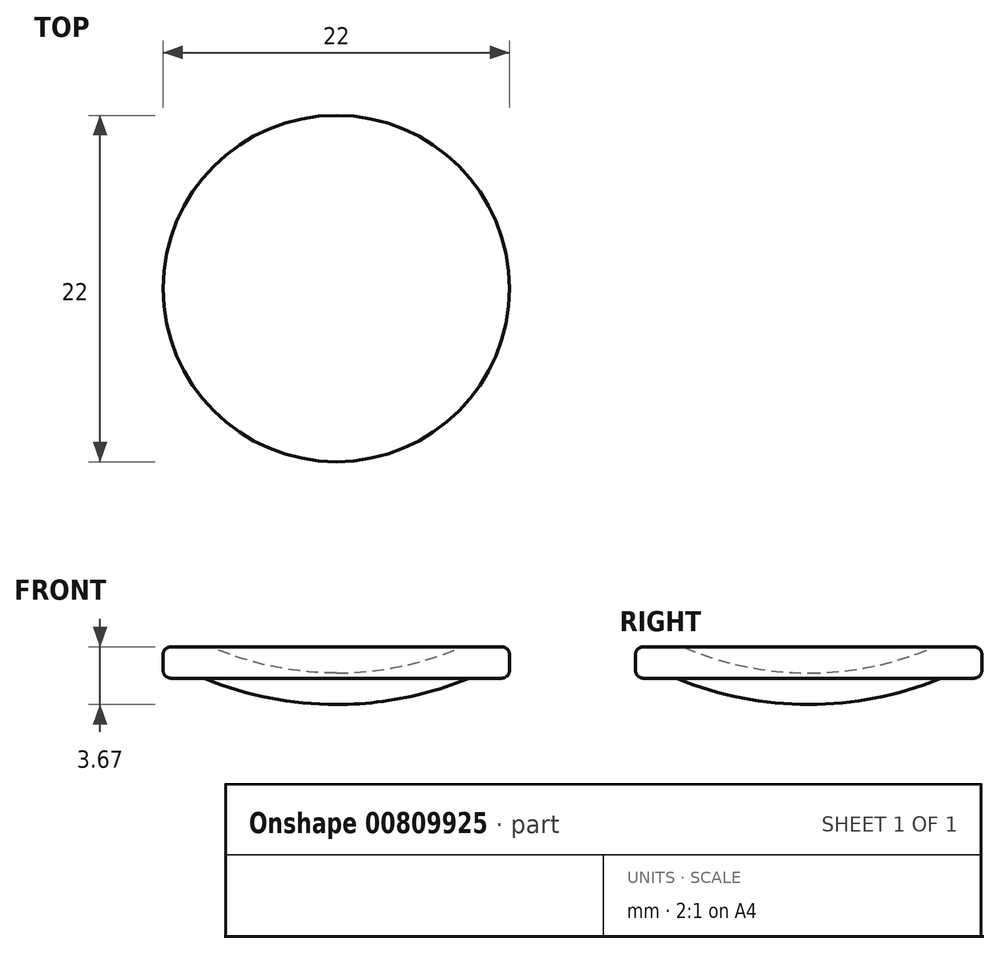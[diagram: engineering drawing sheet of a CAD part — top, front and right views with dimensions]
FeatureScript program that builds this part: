
annotation { "Feature Type Name" : "Feature", "Feature Type Description" : "" }
export const myFeature = defineFeature(function(context is Context, id is Id, definition is map)
    precondition{}
    {
        {
            var Q0;
            Q0=qCreatedBy(makeId("Front.planeOp"),FACE);
            var sketch = newSketch(context, id + "F0", { "sketchPlane" : qUnion([Q0])});
            skArc(sketch, "E0", {"start": v(0, 2) * mm, "mid": v(4.09, 2.42) * mm, "end": v(8, 3.67) * mm});
            skLineSegment(sketch, "E1", {"start": v(8, 3.67) * mm, "end": v(11, 3.67) * mm});
            skLineSegment(sketch, "E2", {"start": v(11, 3.67) * mm, "end": v(11, 1.67) * mm});
            skArc(sketch, "E3.0", {"start": v(0, 0) * mm, "mid": v(4.29, 0.42) * mm, "end": v(8.4, 1.67) * mm});
            skLineSegment(sketch, "E4", {"start": v(11, 1.67) * mm, "end": v(8.4, 1.67) * mm});
            skLineSegment(sketch, "E5", {"start": v(0, 2) * mm, "end": v(0, 0) * mm});
            skSolve(sketch);
        }
        {
            var Q0;
            Q0=makeQuery(id+"F0.imprint","IMPRINT",FACE,{"disambiguationData":[TD([[makeQuery(id+"F0.imprint","IMPRINT",EDGE,{"derivedFrom":sQuery(id+"F0.wireOp",EDGE,"E0")}),-1.0]])]});
            var Q1;
            Q1=sQuery(id+"F0.wireOp",EDGE,"E5");
            revolve(context, id + "F1", {"surfaceOperationType" : NewSurfaceOperationType.NEW, "entities" : qUnion([Q0]), "axis" : qUnion([Q1]), "revolveType" : RevolveType.FULL});
        }
        {
            var Q0;
            Q0=makeQuery(id+"F1.opRevolve","SWEPT_EDGE",EDGE,{"disambiguationData":[OSD([sQuery(id+"F0.wireOp",EDGE,"E1"),sQuery(id+"F0.wireOp",EDGE,"E2")])]});
            var Q1;
            Q1=makeQuery(id+"F1.opRevolve","SWEPT_EDGE",EDGE,{"disambiguationData":[OSD([sQuery(id+"F0.wireOp",EDGE,"E0"),sQuery(id+"F0.wireOp",EDGE,"E1")])]});
            var Q2;
            Q2=makeQuery(id+"F1.opRevolve","SWEPT_EDGE",EDGE,{"disambiguationData":[OSD([sQuery(id+"F0.wireOp",EDGE,"E2"),sQuery(id+"F0.wireOp",EDGE,"E4")])]});
            var Q3;
            Q3=makeQuery(id+"F1.opRevolve","SWEPT_EDGE",EDGE,{"disambiguationData":[OSD([sQuery(id+"F0.wireOp",EDGE,"E3.0"),sQuery(id+"F0.wireOp",EDGE,"E4")])]});
            fillet(context, id + "F2", {"entities" : qUnion([Q0, Q1, Q2, Q3]), "radius" : 0.5 * mm, "tangentPropagation" : true, "allowEdgeOverflow" : false});
        }
    });
